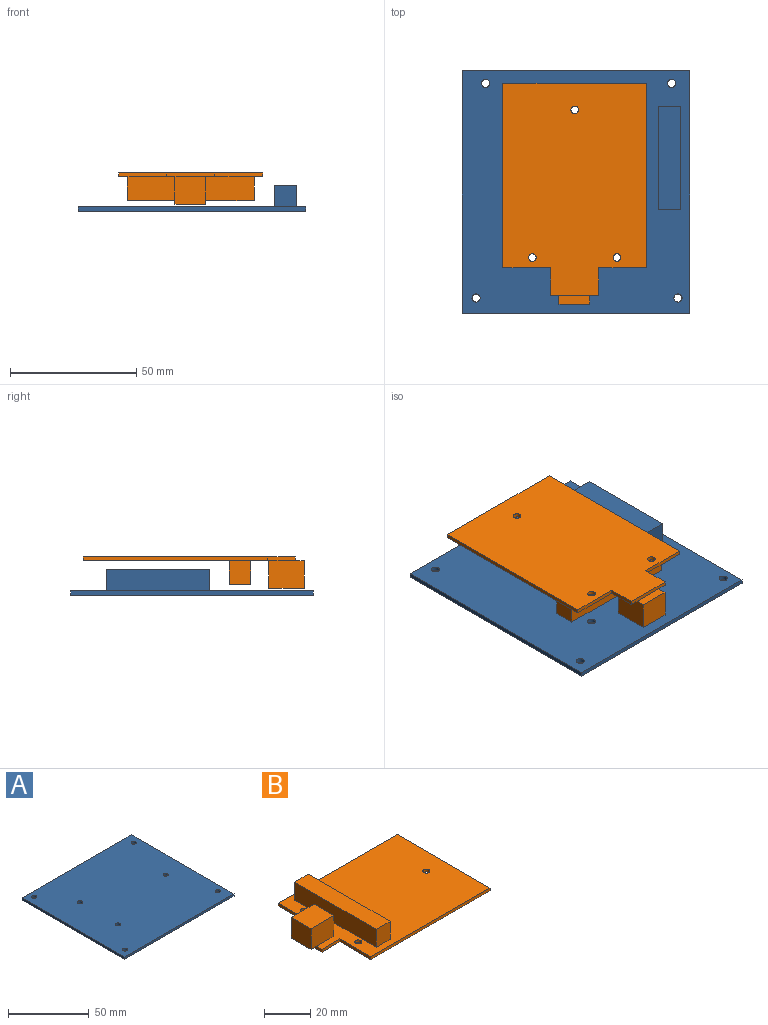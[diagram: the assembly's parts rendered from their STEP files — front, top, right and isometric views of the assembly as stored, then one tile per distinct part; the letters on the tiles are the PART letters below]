
ASSEMBLY  parts=2 mates=1
PART A: 18 faces, bbox 96x90x10.2 mm
  f0: plane 96x90mm, normal (0,0,-1), area 8214.7mm2, adj f2,f3,f4,f5,f6,f7,f8,f9
  f1: plane 96x90mm, normal (0,0,1), area 8583.7mm2, adj f2,f3,f4,f5,f6,f7,f8,f9
  f2: plane 90x1.7mm, normal (-1,0,0), area 153mm2, adj f0,f1,f3,f5
  f3: plane 96x1.7mm, normal (0,-1,0), area 163.2mm2, adj f0,f1,f2,f4
  f4: plane 90x1.7mm, normal (1,0,0), area 153mm2, adj f0,f1,f3,f5
  f5: plane 96x1.7mm, normal (0,1,0), area 163.2mm2, adj f0,f1,f2,f4
  f6: cylinder r=1.6mm len=3.2mm, axis (0,0,-1), area 17.1mm2, adj f0,f1
  f7: cylinder r=1.6mm len=3.2mm, axis (0,0,-1), area 17.1mm2, adj f0,f1
  f8: cylinder r=1.6mm len=3.2mm, axis (0,0,-1), area 17.1mm2, adj f0,f1
  f9: cylinder r=1.6mm len=3.2mm, axis (0,0,-1), area 17.1mm2, adj f0,f1
  f10: cylinder r=1.6mm len=3.2mm, axis (0,0,1), area 17.1mm2, adj f0,f1
  f11: cylinder r=1.6mm len=3.2mm, axis (0,0,1), area 17.1mm2, adj f0,f1
  f12: cylinder r=1.6mm len=3.2mm, axis (0,0,1), area 17.1mm2, adj f0,f1
  f13: plane 9x8.5mm, normal (-1,0,0), area 76.5mm2, adj f0,f14,f16,f17
  f14: plane 41x8.5mm, normal (0,1,0), area 348.5mm2, adj f0,f13,f15,f17
  f15: plane 9x8.5mm, normal (1,0,0), area 76.5mm2, adj f0,f14,f16,f17
  f16: plane 41x8.5mm, normal (0,-1,0), area 348.5mm2, adj f0,f13,f15,f17
  f17: plane 41x9mm, normal (0,0,-1), area 369mm2, adj f13,f14,f15,f16
PART B: 24 faces, bbox 87.5x57x12.5 mm
  f0: plane 84x57mm, normal (0,0,1), area 3794mm2, adj f1,f2,f3,f4,f5,f6,f7,f8
  f1: plane 19x1.5mm, normal (-1,0,0), area 28.5mm2, adj f0,f2,f8,f9
  f2: plane 73x1.5mm, normal (0,-1,0), area 109.5mm2, adj f0,f1,f3,f9
  f3: plane 57x1.5mm, normal (1,0,0), area 85.5mm2, adj f0,f2,f4,f9
  f4: plane 73x1.5mm, normal (0,1,0), area 109.5mm2, adj f0,f3,f5,f9
  f5: plane 19x1.5mm, normal (-1,0,0), area 28.5mm2, adj f0,f4,f6,f9
  f6: plane 11x1.5mm, normal (0,1,0), area 16.5mm2, adj f0,f5,f7,f9
  f7: plane 19x1.5mm, normal (-1,0,0), area 28.5mm2, adj f0,f6,f8,f9,f13
  f8: plane 11x1.5mm, normal (0,-1,0), area 16.5mm2, adj f0,f1,f7,f9
  f9: plane 84x57mm, normal (0,0,-1), area 4348.8mm2, adj f1,f2,f3,f4,f5,f6,f7,f8
  f10: cylinder r=1.5mm len=3mm, axis (0,0,1), area 14.1mm2, adj f0,f9
  f11: cylinder r=1.5mm len=3mm, axis (0,0,1), area 14.1mm2, adj f0,f9
  f12: cylinder r=1.5mm len=3mm, axis (0,0,1), area 14.1mm2, adj f0,f9
  f13: plane 12.11x3.5mm, normal (0,0,-1), area 42.4mm2, adj f7,f14,f15,f17
  f14: plane 12.11x11mm, normal (-1,0,0), area 133.2mm2, adj f13,f15,f17,f18
  f15: plane 14.08x11mm, normal (0,-1,0), area 154.9mm2, adj f0,f13,f14,f16,f18
  f16: plane 12.11x11mm, normal (1,0,0), area 133.2mm2, adj f0,f15,f17,f18
  f17: plane 14.08x11mm, normal (0,1,0), area 154.9mm2, adj f0,f13,f14,f16,f18
  f18: plane 14.08x12.11mm, normal (0,0,1), area 170.5mm2, adj f14,f15,f16,f17
  f19: plane 50.2x9.5mm, normal (-1,0,0), area 476.9mm2, adj f0,f20,f22,f23
  f20: plane 9.5x8.5mm, normal (0,-1,0), area 80.8mm2, adj f0,f19,f21,f23
  f21: plane 50.2x9.5mm, normal (1,0,0), area 476.9mm2, adj f0,f20,f22,f23
  f22: plane 9.5x8.5mm, normal (0,1,0), area 80.8mm2, adj f0,f19,f21,f23
  f23: plane 50.2x8.5mm, normal (0,0,1), area 426.7mm2, adj f19,f20,f21,f22
PLACE A rot(axis=(-0.71,-0.71,0),180deg) t=(-93.02,-65.73,13.6)mm
PLACE B rot(axis=(-0.71,-0.71,0),180deg) t=(-77.02,-47.73,27.1)mm
MATE fastened A.f10 <-> B.f11  axis (0,0,1) through (-31.77,-43.73,13.6)mm
